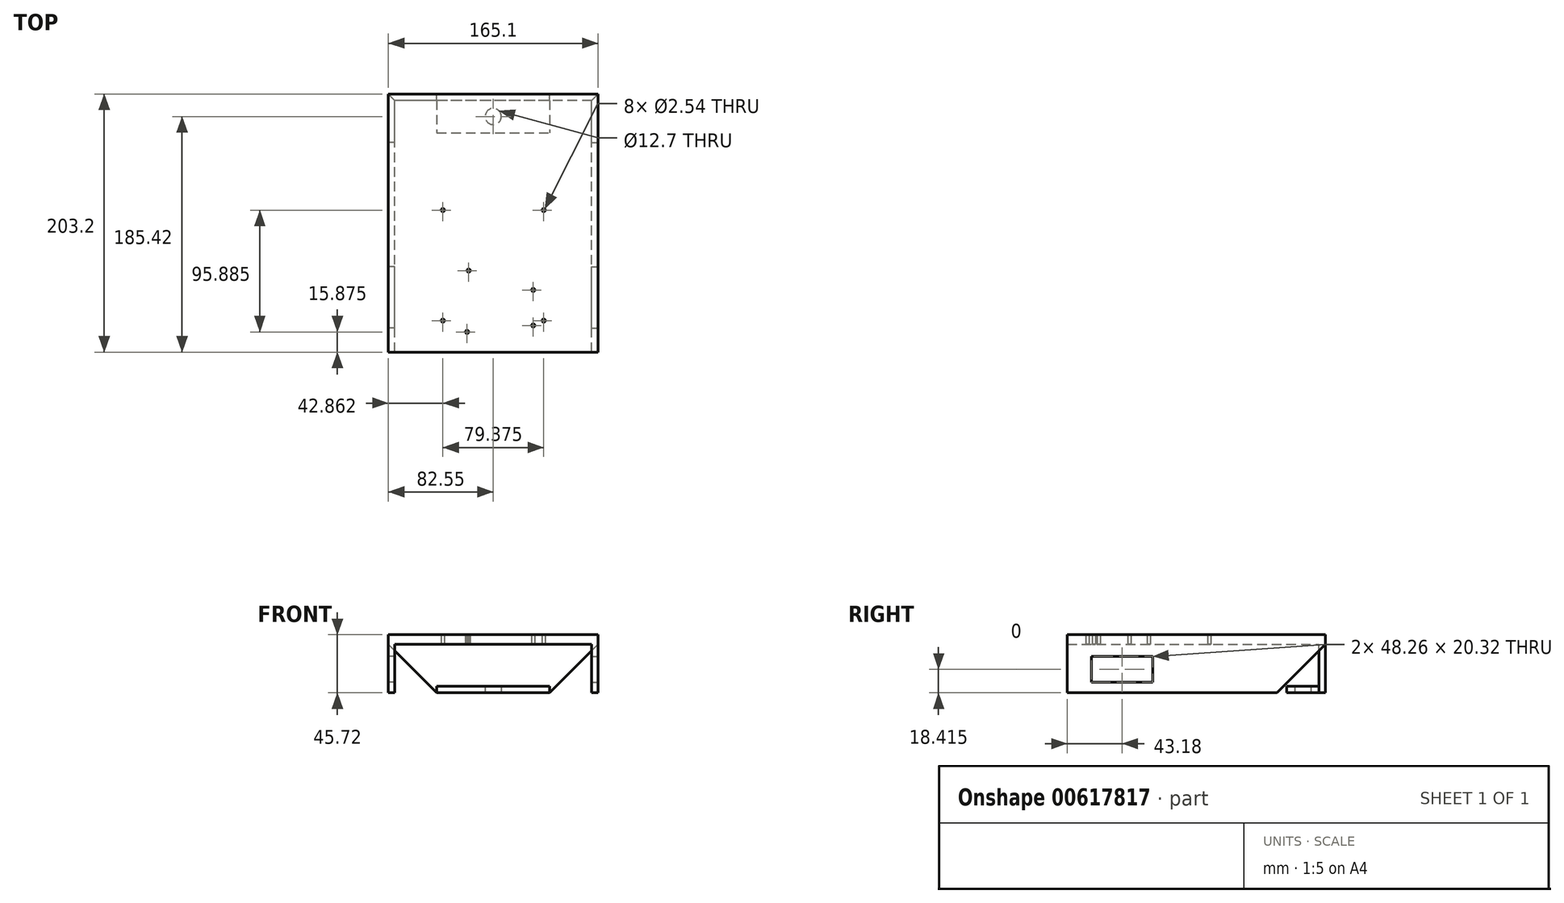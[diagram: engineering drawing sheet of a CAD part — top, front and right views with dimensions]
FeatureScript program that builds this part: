
annotation { "Feature Type Name" : "Feature", "Feature Type Description" : "" }
export const myFeature = defineFeature(function(context is Context, id is Id, definition is map)
    precondition{}
    {
        {
            var Q0;
            Q0=qCreatedBy(makeId("Top.planeOp"),FACE);
            var sketch = newSketch(context, id + "F0", { "sketchPlane" : qUnion([Q0])});
            skLineSegment(sketch, "E0.bottom", {"start": v(82.55, -101.6) * mm, "end": v(-82.55, -101.6) * mm});
            skLineSegment(sketch, "E0.top", {"start": v(82.55, 101.6) * mm, "end": v(-82.55, 101.6) * mm});
            skLineSegment(sketch, "E0.left", {"start": v(82.55, -101.6) * mm, "end": v(82.55, 101.6) * mm});
            skLineSegment(sketch, "E0.right", {"start": v(-82.55, -101.6) * mm, "end": v(-82.55, 101.6) * mm});
            skPoint(sketch, "E0.middle", {"position": v(0, 0) * mm});
            skPoint(sketch, "E1", {"position": v(-46.04, -92.08) * mm});
            skPoint(sketch, "E2", {"position": v(-46.04, 25.4) * mm});
            skPoint(sketch, "E3", {"position": v(46.04, 25.4) * mm});
            skCircle(sketch, "E4", {"center": v(-39.69, -76.84) * mm, "radius": 1.27 * mm});
            skLineSegment(sketch, "E5", {"start": v(0, 0) * mm, "end": v(0, -66.8) * mm});
            skPoint(sketch, "E6.MirrorP", {"position": v(46.04, -92.08) * mm});
            skCircle(sketch, "E7.MirrorC", {"center": v(39.69, -76.84) * mm, "radius": 1.27 * mm});
            skLineSegment(sketch, "E8", {"start": v(0, -33.34) * mm, "end": v(-57.42, -33.34) * mm});
            skCircle(sketch, "E9.MirrorC", {"center": v(39.69, 10.16) * mm, "radius": 1.27 * mm});
            skCircle(sketch, "E10.MirrorC", {"center": v(-39.69, 10.16) * mm, "radius": 1.27 * mm});
            skCircle(sketch, "E11", {"center": v(-20.64, -85.73) * mm, "radius": 1.27 * mm});
            skCircle(sketch, "E12", {"center": v(31.43, -80.64) * mm, "radius": 1.27 * mm});
            skCircle(sketch, "E13", {"center": v(-19.37, -37.47) * mm, "radius": 1.27 * mm});
            skCircle(sketch, "E14", {"center": v(31.43, -52.7) * mm, "radius": 1.27 * mm});
            skSolve(sketch);
        }
        {
            var Q0;
            Q0=makeQuery(id+"F0.imprint","IMPRINT",FACE,{"disambiguationData":[TD([[makeQuery(id+"F0.imprint","IMPRINT",EDGE,{"derivedFrom":sQuery(id+"F0.wireOp",EDGE,"E0.bottom")}),-1.0]])]});
            extrude(context, id + "F1", {"entities" : qUnion([Q0]), "depth" : 7.62 * mm, "offsetDistance" : 25.4 * mm});
        }
        {
            var Q0;
            Q0=makeQuery(id+"F1.opExtrude","SWEPT_FACE",FACE,{"disambiguationData":[OSD([sQuery(id+"F0.wireOp",EDGE,"E0.left")])]});
            var sketch = newSketch(context, id + "F2", { "sketchPlane" : qUnion([Q0])});
            skLineSegment(sketch, "E15.bottom", {"start": v(-101.6, 0) * mm, "end": v(63.5, 0) * mm});
            skLineSegment(sketch, "E15.top", {"start": v(-101.6, -38.1) * mm, "end": v(63.5, -38.1) * mm});
            skLineSegment(sketch, "E15.left", {"start": v(-101.6, 0) * mm, "end": v(-101.6, -38.1) * mm});
            skLineSegment(sketch, "E15.right", {"start": v(63.5, 0) * mm, "end": v(63.5, -38.1) * mm});
            skLineSegment(sketch, "E16", {"start": v(63.5, -38.1) * mm, "end": v(101.6, 0) * mm});
            skLineSegment(sketch, "E17.bottom", {"start": v(-82.55, -9.53) * mm, "end": v(-34.3, -9.53) * mm});
            skLineSegment(sketch, "E17.top", {"start": v(-82.55, -29.84) * mm, "end": v(-34.3, -29.84) * mm});
            skLineSegment(sketch, "E17.left", {"start": v(-82.55, -9.53) * mm, "end": v(-82.55, -29.84) * mm});
            skLineSegment(sketch, "E17.right", {"start": v(-34.3, -9.53) * mm, "end": v(-34.3, -29.85) * mm});
            skSolve(sketch);
        }
        {
            var Q0;
            Q0 = qSketchRegion(id + "F2", true);
            var Q1;
            {var subQ0=sQuery(id+"F2.wireOp",EDGE,"E15.right");Q1=makeQuery(id+"F2.imprint","IMPRINT",FACE,{"disambiguationData":[TD([[makeQuery(id+"F2.imprint","IMPRINT",EDGE,{"derivedFrom":subQ0}),1.0]])]});}
            extrude(context, id + "F3", {"entities" : qUnion([Q0, Q1]), "oppositeDirection" : true, "depth" : 5.08 * mm, "offsetDistance" : 25.4 * mm});
        }
        {
            var Q0;
            Q0=makeQuery(id+"F3.opExtrude","SWEPT_BODY",BODY,{"disambiguationData":[OSD([sQuery(id+"F0.wireOp",EDGE,"E0.left"),sQuery(id+"F2.wireOp",EDGE,"E15.bottom"),sQuery(id+"F2.wireOp",EDGE,"E15.top"),sQuery(id+"F2.wireOp",EDGE,"E15.left"),sQuery(id+"F2.wireOp",EDGE,"E16"),sQuery(id+"F2.wireOp",EDGE,"E17.bottom"),sQuery(id+"F2.wireOp",EDGE,"E17.top"),sQuery(id+"F2.wireOp",EDGE,"E17.left"),sQuery(id+"F2.wireOp",EDGE,"E17.right")])]});
            var Q1;
            Q1=qCreatedBy(makeId("Right.planeOp"),FACE);
            mirror(context, id + "F4", {"operationType" : NewBodyOperationType.ADD, "entities" : qUnion([Q0]), "mirrorPlane" : qUnion([Q1])});
        }
        {
            var Q0;
            Q0=makeQuery(id+"F1.opExtrude","SWEPT_FACE",FACE,{"disambiguationData":[OSD([sQuery(id+"F0.wireOp",EDGE,"E0.top")])]});
            var sketch = newSketch(context, id + "F5", { "sketchPlane" : qUnion([Q0])});
            skLineSegment(sketch, "E18", {"start": v(-82.55, 0) * mm, "end": v(-44.45, -38.1) * mm});
            skLineSegment(sketch, "E19", {"start": v(-44.45, -38.1) * mm, "end": v(44.45, -38.1) * mm});
            skLineSegment(sketch, "E20", {"start": v(44.45, -38.1) * mm, "end": v(82.55, 0) * mm});
            skSolve(sketch);
        }
        {
            var Q0;
            Q0=makeQuery(id+"F5.imprint","IMPRINT",FACE,{"disambiguationData":[TD([[makeQuery(id+"F5.imprint","IMPRINT",EDGE,{"derivedFrom":sQuery(id+"F5.wireOp",EDGE,"E18")}),1.0]])]});
            extrude(context, id + "F6", {"entities" : qUnion([Q0]), "operationType" : NewBodyOperationType.ADD, "oppositeDirection" : true, "depth" : 5.08 * mm, "offsetDistance" : 25.4 * mm});
        }
        {
            var Q0;
            Q0=makeQuery(id+"F6.opExtrude","SWEPT_FACE",FACE,{"disambiguationData":[OSD([sQuery(id+"F5.wireOp",EDGE,"E19")])]});
            var sketch = newSketch(context, id + "F7", { "sketchPlane" : qUnion([Q0])});
            skLineSegment(sketch, "E21.bottom", {"start": v(-44.45, -96.52) * mm, "end": v(44.45, -96.52) * mm});
            skLineSegment(sketch, "E21.top", {"start": v(-44.45, -71.12) * mm, "end": v(44.45, -71.12) * mm});
            skLineSegment(sketch, "E21.left", {"start": v(-44.45, -96.52) * mm, "end": v(-44.45, -71.12) * mm});
            skLineSegment(sketch, "E21.right", {"start": v(44.45, -96.52) * mm, "end": v(44.45, -71.12) * mm});
            skCircle(sketch, "E22", {"center": v(0, -83.82) * mm, "radius": 6.35 * mm});
            skSolve(sketch);
        }
        {
            var Q0;
            Q0=makeQuery(id+"F7.imprint","IMPRINT",FACE,{"disambiguationData":[TD([[makeQuery(id+"F7.imprint","IMPRINT",EDGE,{"derivedFrom":sQuery(id+"F7.wireOp",EDGE,"E21.bottom")}),-1.0]])]});
            extrude(context, id + "F8", {"entities" : qUnion([Q0]), "operationType" : NewBodyOperationType.ADD, "oppositeDirection" : true, "depth" : 5.08 * mm, "offsetDistance" : 25.4 * mm});
        }
    });
